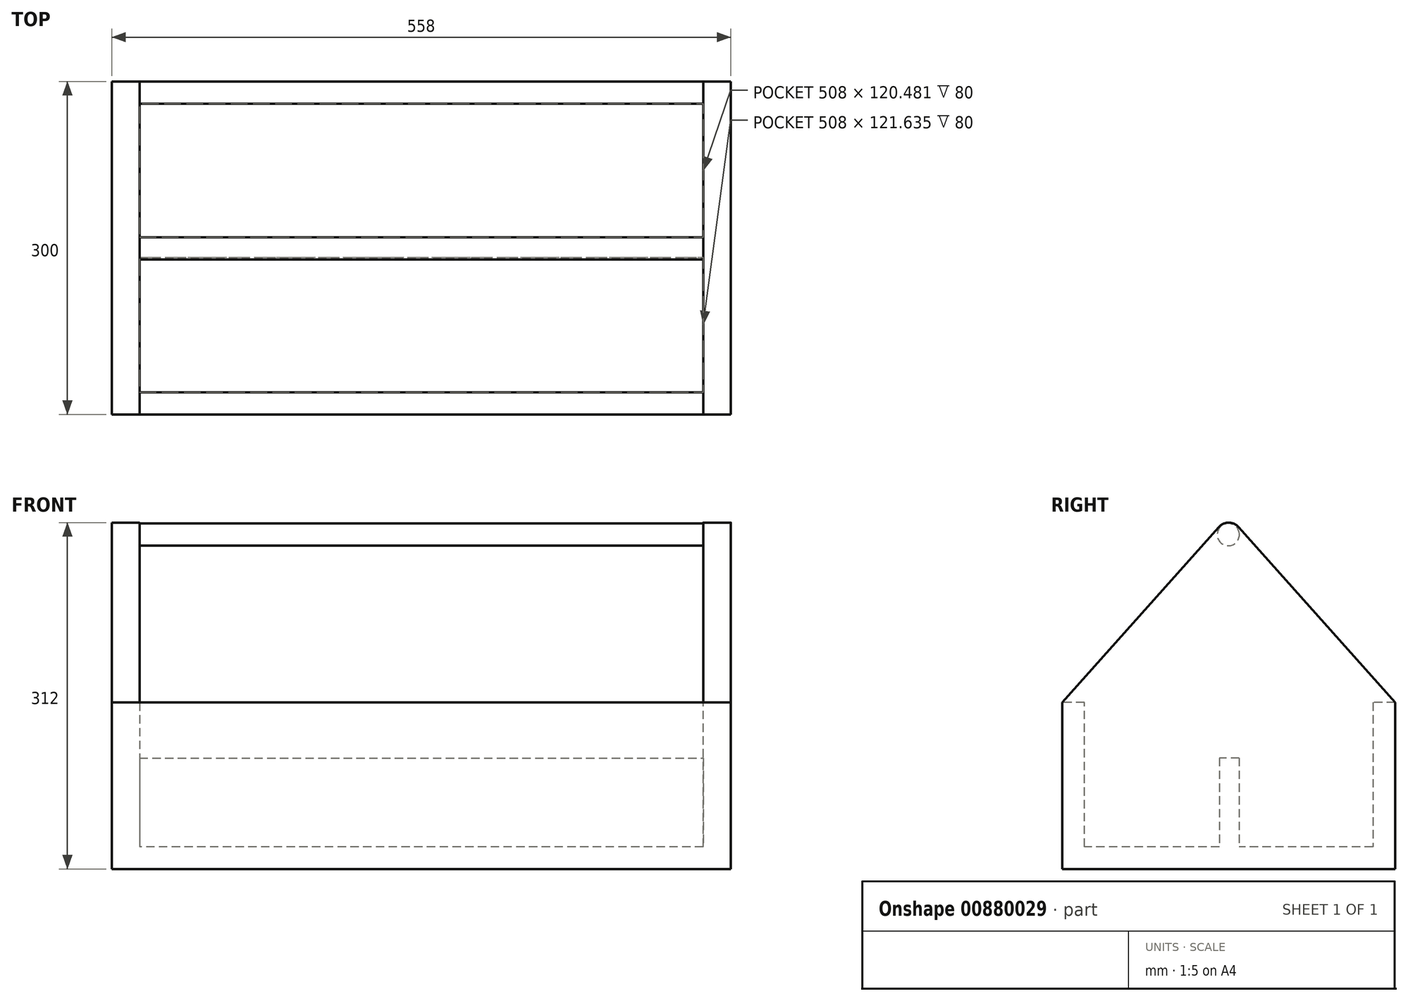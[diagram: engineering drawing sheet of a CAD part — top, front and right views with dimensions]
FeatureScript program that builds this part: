
annotation { "Feature Type Name" : "Feature", "Feature Type Description" : "" }
export const myFeature = defineFeature(function(context is Context, id is Id, definition is map)
    precondition{}
    {
        {
            var Q0;
            Q0=qCreatedBy(makeId("Right.planeOp"),FACE);
            var sketch = newSketch(context, id + "F0", { "sketchPlane" : qUnion([Q0])});
            skLineSegment(sketch, "E0", {"start": v(-97.45, -26.33) * mm, "end": v(202.55, -26.33) * mm});
            skLineSegment(sketch, "E1", {"start": v(202.55, 123.67) * mm, "end": v(202.55, -26.33) * mm});
            skLineSegment(sketch, "E2", {"start": v(-97.45, -26.33) * mm, "end": v(-97.45, 123.67) * mm});
            skArc(sketch, "E3", {"start": v(61.5, 281.66) * mm, "mid": v(52.55, 285.67) * mm, "end": v(43.6, 281.66) * mm});
            skPoint(sketch, "E3.centerSnap0", {"position": v(52.55, -26.33) * mm});
            skLineSegment(sketch, "E4", {"start": v(-97.45, 123.67) * mm, "end": v(43.6, 281.66) * mm});
            skLineSegment(sketch, "E5", {"start": v(202.55, 123.67) * mm, "end": v(61.5, 281.66) * mm});
            skSolve(sketch);
        }
        {
            var Q0;
            Q0=qSketchRegion(id+"F0",true);
            extrude(context, id + "F1", {"entities" : qUnion([Q0]), "depth" : 25 * mm, "offsetDistance" : 25 * mm});
        }
        {
            var Q0;
            Q0=makeQuery(id+"F1.opExtrude","CAP_FACE",FACE,{"disambiguationData":[OSD([sQuery(id+"F0.wireOp",EDGE,"E0"),sQuery(id+"F0.wireOp",EDGE,"E1"),sQuery(id+"F0.wireOp",EDGE,"E2"),sQuery(id+"F0.wireOp",EDGE,"E3"),sQuery(id+"F0.wireOp",EDGE,"E4"),sQuery(id+"F0.wireOp",EDGE,"E5")])],"isStart":true});
            var sketch = newSketch(context, id + "F2", { "sketchPlane" : qUnion([Q0])});
            skLineSegment(sketch, "E6", {"start": v(-202.55, 123.67) * mm, "end": v(-182.55, 123.67) * mm});
            skLineSegment(sketch, "E7", {"start": v(-182.55, 123.67) * mm, "end": v(-182.55, -6.33) * mm});
            skLineSegment(sketch, "E8", {"start": v(-182.55, -6.33) * mm, "end": v(77.45, -6.33) * mm});
            skLineSegment(sketch, "E9", {"start": v(97.45, 123.67) * mm, "end": v(97.45, 123.67) * mm});
            skLineSegment(sketch, "E10", {"start": v(77.45, -6.33) * mm, "end": v(77.45, 123.67) * mm});
            skLineSegment(sketch, "E11", {"start": v(77.45, 123.67) * mm, "end": v(97.45, 123.67) * mm});
            skSolve(sketch);
        }
        {
            var Q0;
            Q0=qSketchRegion(id+"F2",true);
            var Q1;
            Q1=makeQuery(id+"F2.imprint","IMPRINT",FACE,{"disambiguationData":[TD([[makeQuery(id+"F2.imprint","IMPRINT",EDGE,{"derivedFrom":sQuery(id+"F2.wireOp",EDGE,"E6")}),-1.0]])]});
            extrude(context, id + "F3", {"entities" : qUnion([Q0, Q1]), "operationType" : NewBodyOperationType.ADD, "depth" : 508 * mm, "offsetDistance" : 25 * mm});
        }
        {
            var Q0;
            Q0=makeQuery(id+"F3.opExtrude","CAP_FACE",FACE,{"disambiguationData":[OSD([sQuery(id+"F0.wireOp",EDGE,"E0"),sQuery(id+"F0.wireOp",EDGE,"E1"),sQuery(id+"F0.wireOp",EDGE,"E2"),sQuery(id+"F2.wireOp",EDGE,"E6"),sQuery(id+"F2.wireOp",EDGE,"E7"),sQuery(id+"F2.wireOp",EDGE,"E8"),sQuery(id+"F2.wireOp",EDGE,"NgHp8GeH-2828-YXRl-GsCZ-DGXQ4YvgHPgH"),sQuery(id+"F2.wireOp",EDGE,"E9")])],"isStart":false});
            var sketch = newSketch(context, id + "F4", { "sketchPlane" : qUnion([Q0])});
            skArc(sketch, "E12", {"start": v(-43.6, 281.66) * mm, "mid": v(-52.55, 285.67) * mm, "end": v(-61.5, 281.66) * mm});
            skLineSegment(sketch, "E13", {"start": v(-202.55, 123.67) * mm, "end": v(-61.5, 281.66) * mm});
            skLineSegment(sketch, "E14", {"start": v(97.45, 123.67) * mm, "end": v(-43.6, 281.66) * mm});
            skLineSegment(sketch, "E15", {"start": v(97.45, 123.67) * mm, "end": v(97.45, -26.33) * mm});
            skLineSegment(sketch, "E16", {"start": v(97.45, -26.33) * mm, "end": v(-202.55, -26.33) * mm});
            skLineSegment(sketch, "E17", {"start": v(-202.55, -26.33) * mm, "end": v(-202.55, 123.67) * mm});
            skSolve(sketch);
        }
        {
            var Q0;
            Q0=qSketchRegion(id+"F4",true);
            extrude(context, id + "F5", {"entities" : qUnion([Q0]), "operationType" : NewBodyOperationType.ADD, "depth" : 25 * mm, "offsetDistance" : 25 * mm});
        }
        {
            var Q0;
            Q0=makeQuery(id+"F0.imprint","IMPRINT",FACE,{"disambiguationData":[TD([[makeQuery(id+"F0.imprint","IMPRINT",EDGE,{"derivedFrom":sQuery(id+"F0.wireOp",EDGE,"E0")}),1.0]])]});
            var sketch = newSketch(context, id + "F6", { "sketchPlane" : qUnion([Q0])});
            skCircle(sketch, "E18", {"center": v(52.24, 274.9) * mm, "radius": 10 * mm});
            skSolve(sketch);
        }
        {
            var Q0;
            Q0=qSketchRegion(id+"F6",true);
            extrude(context, id + "F7", {"entities" : qUnion([Q0]), "operationType" : NewBodyOperationType.ADD, "oppositeDirection" : true, "depth" : 508 * mm, "offsetDistance" : 25 * mm});
        }
        {
            var Q0;
            Q0=makeQuery(id+"F3.opExtrude","SWEPT_FACE",FACE,{"disambiguationData":[OSD([sQuery(id+"F2.wireOp",EDGE,"E8")])]});
            var sketch = newSketch(context, id + "F8", { "sketchPlane" : qUnion([Q0])});
            skLineSegment(sketch, "E19", {"start": v(-508, 44.18) * mm, "end": v(0, 44.18) * mm});
            skLineSegment(sketch, "E20", {"start": v(0, 44.18) * mm, "end": v(0, 62.07) * mm});
            skLineSegment(sketch, "E21", {"start": v(0, 62.07) * mm, "end": v(-508, 62.07) * mm});
            skLineSegment(sketch, "E22", {"start": v(-508, 62.07) * mm, "end": v(-508, 44.18) * mm});
            skSolve(sketch);
        }
        {
            var Q0;
            Q0=makeQuery(id+"F8.imprint","IMPRINT",FACE,{"disambiguationData":[TD([[makeQuery(id+"F8.imprint","IMPRINT",EDGE,{"derivedFrom":sQuery(id+"F8.wireOp",EDGE,"E19")}),1.0]])]});
            extrude(context, id + "F9", {"entities" : qUnion([Q0]), "operationType" : NewBodyOperationType.ADD, "depth" : 80 * mm, "offsetDistance" : 25 * mm});
        }
    });
